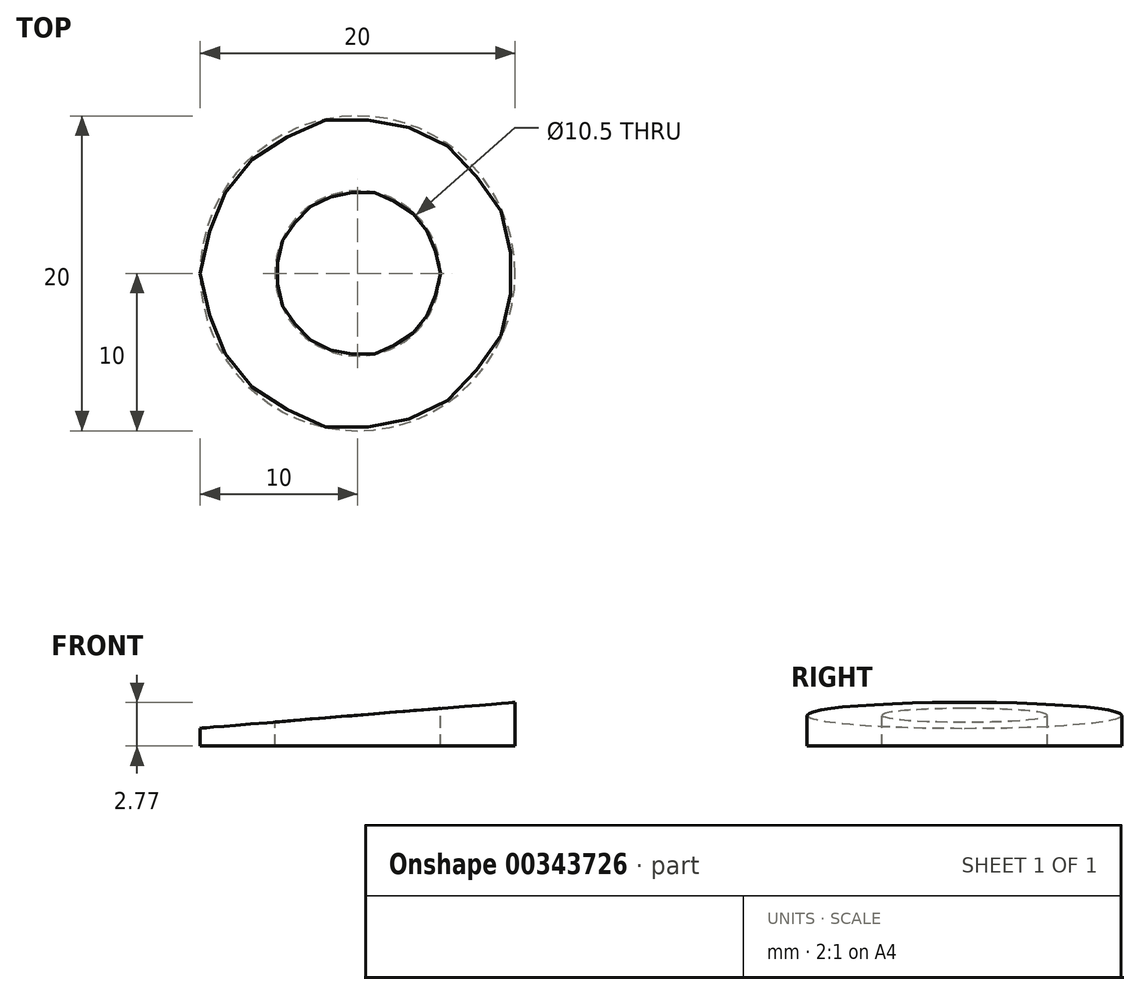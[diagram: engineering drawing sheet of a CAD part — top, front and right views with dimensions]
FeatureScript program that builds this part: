
annotation { "Feature Type Name" : "Feature", "Feature Type Description" : "" }
export const myFeature = defineFeature(function(context is Context, id is Id, definition is map)
    precondition{}
    {
        {
            var Q0;
            Q0=qCreatedBy(makeId("Top.planeOp"),FACE);
            var sketch = newSketch(context, id + "F0", { "sketchPlane" : qUnion([Q0])});
            skCircle(sketch, "E0", {"center": v(0, 0) * mm, "radius": 10 * mm});
            skSolve(sketch);
        }
        {
            var Q0;
            Q0 = qSketchRegion(id + "F0", true);
            extrude(context, id + "F1", {"entities" : qUnion([Q0]), "depth" : 5 * mm});
        }
        {
            var Q0;
            Q0=makeQuery(id+"F1.opExtrude","CAP_FACE",FACE,{"disambiguationData":[OSD([sQuery(id+"F0.wireOp",EDGE,"E0")])],"isStart":false});
            var sketch = newSketch(context, id + "F2", { "sketchPlane" : qUnion([Q0])});
            skCircle(sketch, "E1", {"center": v(0, 0) * mm, "radius": 5.25 * mm});
            skSolve(sketch);
        }
        {
            var Q0;
            Q0 = qSketchRegion(id + "F2", true);
            extrude(context, id + "F3", {"entities" : qUnion([Q0]), "operationType" : NewBodyOperationType.REMOVE, "endBound" : BoundingType.THROUGH_ALL, "oppositeDirection" : true, "depth" : 25 * mm});
        }
        {
            var Q0;
            Q0=qCreatedBy(makeId("Front.planeOp"),FACE);
            cPlane(context, id + "F4", {"entities" : qUnion([Q0]), "cplaneType" : CPlaneType.OFFSET, "offset" : 25 * mm, "width" : 150 * mm, "height" : 150 * mm});
        }
        {
            var Q0;
            Q0=qCreatedBy(id+"F4.planeOp",FACE);
            var sketch = newSketch(context, id + "F5", { "sketchPlane" : qUnion([Q0])});
            skLineSegment(sketch, "E2", {"start": v(-23.74, 0) * mm, "end": v(45.85, 5.72) * mm});
            skLineSegment(sketch, "E3", {"start": v(45.85, 5.72) * mm, "end": v(-11.63, 5.72) * mm});
            skLineSegment(sketch, "E4", {"start": v(-11.63, 5.72) * mm, "end": v(-23.74, 0) * mm});
            skSolve(sketch);
        }
        {
            var Q0;
            Q0 = qSketchRegion(id + "F5", true);
            extrude(context, id + "F6", {"entities" : qUnion([Q0]), "operationType" : NewBodyOperationType.REMOVE, "oppositeDirection" : true, "depth" : 50 * mm});
        }
    });
